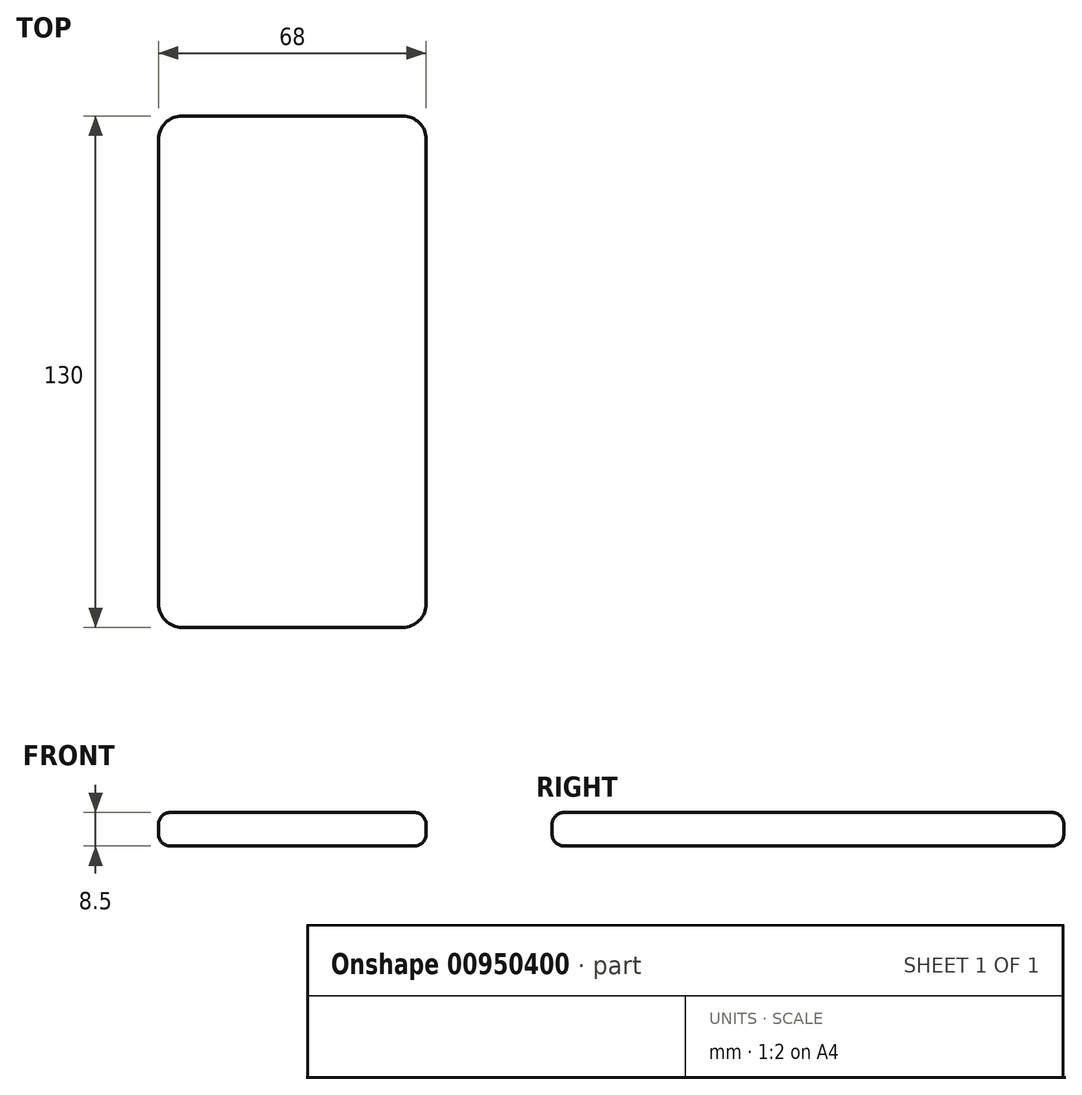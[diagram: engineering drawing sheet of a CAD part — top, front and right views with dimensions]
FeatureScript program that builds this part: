
annotation { "Feature Type Name" : "Feature", "Feature Type Description" : "" }
export const myFeature = defineFeature(function(context is Context, id is Id, definition is map)
    precondition{}
    {
        {
            var Q0;
            Q0=qCreatedBy(makeId("Top.planeOp"),FACE);
            var sketch = newSketch(context, id + "F0", { "sketchPlane" : qUnion([Q0])});
            skLineSegment(sketch, "E0.bottom", {"start": v(0, 0) * mm, "end": v(68, 0) * mm});
            skLineSegment(sketch, "E0.top", {"start": v(0, 130) * mm, "end": v(68, 130) * mm});
            skLineSegment(sketch, "E0.left", {"start": v(0, 0) * mm, "end": v(0, 130) * mm});
            skLineSegment(sketch, "E0.right", {"start": v(68, 0) * mm, "end": v(68, 130) * mm});
            skSolve(sketch);
        }
        {
            var Q0;
            Q0 = qSketchRegion(id + "F0", true);
            extrude(context, id + "F1", {"entities" : qUnion([Q0]), "depth" : 8.5 * mm, "offsetDistance" : 25 * mm});
        }
        {
            var Q0;
            Q0=makeQuery(id+"F1.opExtrude","CAP_EDGE",EDGE,{"disambiguationData":[OSD([sQuery(id+"F0.wireOp",EDGE,"E0.left")])],"isStart":false});
            var Q1;
            Q1=makeQuery(id+"F1.opExtrude","CAP_EDGE",EDGE,{"disambiguationData":[OSD([sQuery(id+"F0.wireOp",EDGE,"E0.left")])],"isStart":true});
            var Q2;
            Q2=makeQuery(id+"F1.opExtrude","CAP_EDGE",EDGE,{"disambiguationData":[OSD([sQuery(id+"F0.wireOp",EDGE,"E0.right")])],"isStart":false});
            var Q3;
            Q3=makeQuery(id+"F1.opExtrude","CAP_EDGE",EDGE,{"disambiguationData":[OSD([sQuery(id+"F0.wireOp",EDGE,"E0.right")])],"isStart":true});
            var Q4;
            Q4=makeQuery(id+"F1.opExtrude","CAP_EDGE",EDGE,{"disambiguationData":[OSD([sQuery(id+"F0.wireOp",EDGE,"E0.bottom")])],"isStart":true});
            var Q5;
            Q5=makeQuery(id+"F1.opExtrude","CAP_EDGE",EDGE,{"disambiguationData":[OSD([sQuery(id+"F0.wireOp",EDGE,"E0.bottom")])],"isStart":false});
            var Q6;
            Q6=makeQuery(id+"F1.opExtrude","CAP_EDGE",EDGE,{"disambiguationData":[OSD([sQuery(id+"F0.wireOp",EDGE,"E0.top")])],"isStart":false});
            var Q7;
            Q7=makeQuery(id+"F1.opExtrude","CAP_EDGE",EDGE,{"disambiguationData":[OSD([sQuery(id+"F0.wireOp",EDGE,"E0.top")])],"isStart":true});
            fillet(context, id + "F2", {"entities" : qUnion([Q0, Q1, Q2, Q3, Q4, Q5, Q6, Q7]), "radius" : 3 * mm, "tangentPropagation" : true, "allowEdgeOverflow" : false});
        }
        {
            var Q0;
            Q0=makeQuery(id+"F1.opExtrude","SWEPT_EDGE",EDGE,{"disambiguationData":[OSD([sQuery(id+"F0.wireOp",EDGE,"E0.bottom"),sQuery(id+"F0.wireOp",EDGE,"E0.left")])]});
            var Q1;
            Q1=makeQuery(id+"F1.opExtrude","SWEPT_EDGE",EDGE,{"disambiguationData":[OSD([sQuery(id+"F0.wireOp",EDGE,"E0.bottom"),sQuery(id+"F0.wireOp",EDGE,"E0.right")])]});
            var Q2;
            Q2=makeQuery(id+"F1.opExtrude","SWEPT_EDGE",EDGE,{"disambiguationData":[OSD([sQuery(id+"F0.wireOp",EDGE,"E0.top"),sQuery(id+"F0.wireOp",EDGE,"E0.right")])]});
            var Q3;
            Q3=makeQuery(id+"F1.opExtrude","SWEPT_EDGE",EDGE,{"disambiguationData":[OSD([sQuery(id+"F0.wireOp",EDGE,"E0.top"),sQuery(id+"F0.wireOp",EDGE,"E0.left")])]});
            fillet(context, id + "F3", {"entities" : qUnion([Q0, Q1, Q2, Q3]), "radius" : 6 * mm, "tangentPropagation" : true, "allowEdgeOverflow" : false});
        }
    });
